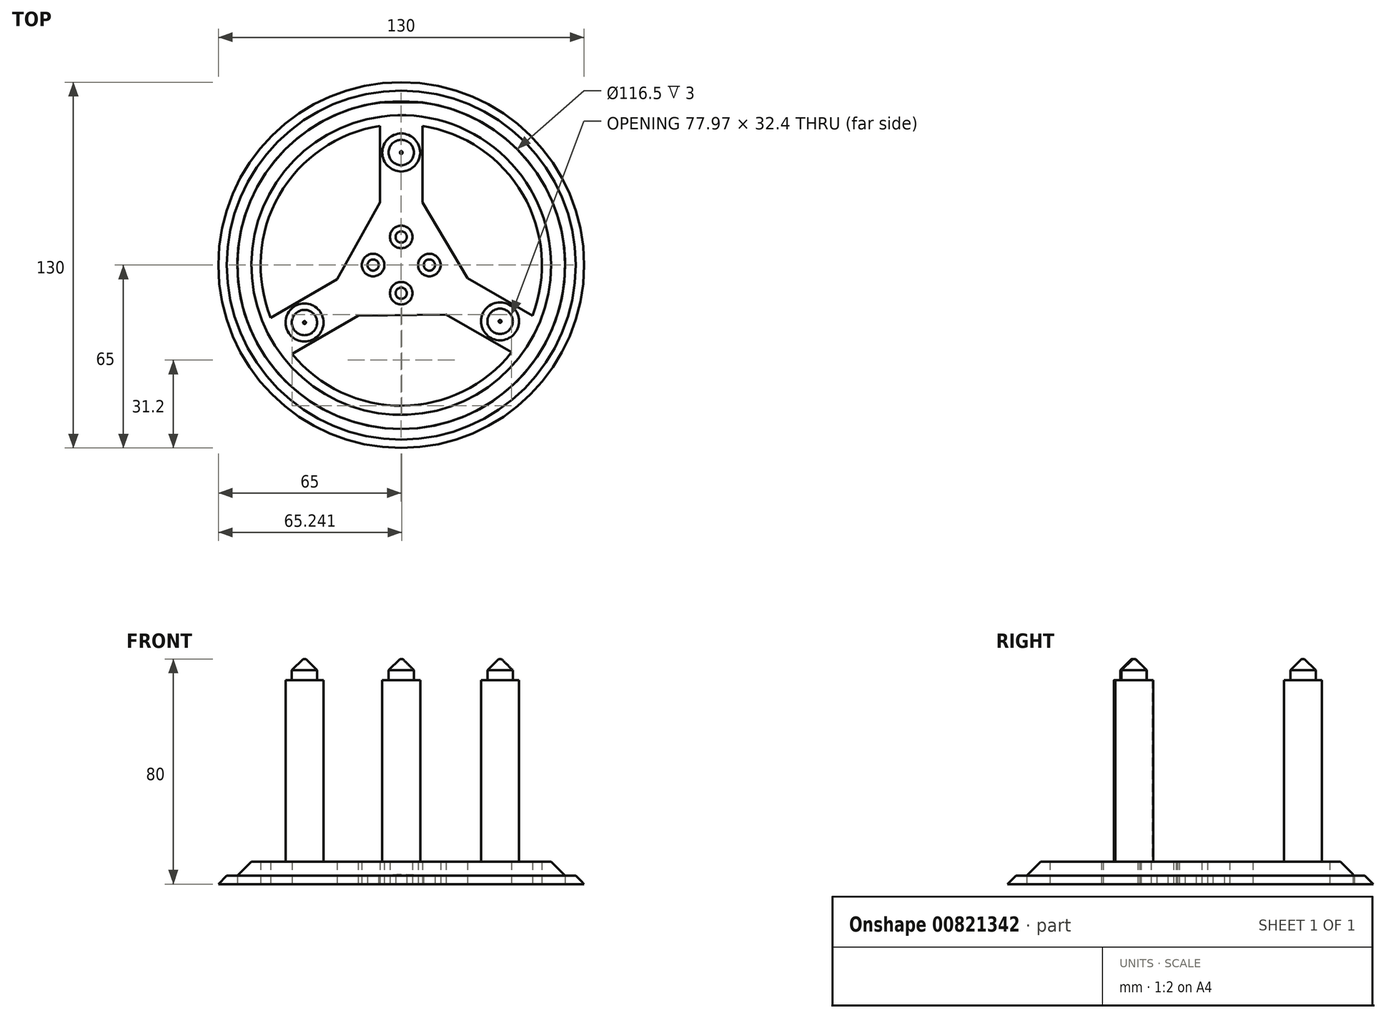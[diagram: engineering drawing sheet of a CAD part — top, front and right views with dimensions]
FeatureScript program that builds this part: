
annotation { "Feature Type Name" : "Feature", "Feature Type Description" : "" }
export const myFeature = defineFeature(function(context is Context, id is Id, definition is map)
    precondition{}
    {
        {
            var Q0;
            Q0=qCreatedBy(makeId("Top.planeOp"),FACE);
            var sketch = newSketch(context, id + "F0", { "sketchPlane" : qUnion([Q0])});
            skCircle(sketch, "E0", {"center": v(0, 0) * mm, "radius": 65 * mm});
            skCircle(sketch, "E1", {"center": v(0, 0) * mm, "radius": 50 * mm});
            skCircle(sketch, "E2", {"center": v(0, 0) * mm, "radius": 58.25 * mm});
            skLineSegment(sketch, "E3", {"start": v(0, 50) * mm, "end": v(0, 40) * mm});
            skCircle(sketch, "E4", {"center": v(0, 40) * mm, "radius": 6.75 * mm});
            skCircle(sketch, "E5", {"center": v(0, 40) * mm, "radius": 7.5 * mm});
            skLineSegment(sketch, "E6.bottom", {"start": v(7.5, 57.77) * mm, "end": v(-7.5, 57.77) * mm});
            skLineSegment(sketch, "E6.top", {"start": v(7.5, 22.23) * mm, "end": v(-7.5, 22.23) * mm});
            skLineSegment(sketch, "E6.left", {"start": v(7.5, 57.77) * mm, "end": v(7.5, 22.23) * mm});
            skLineSegment(sketch, "E6.right", {"start": v(-7.5, 57.77) * mm, "end": v(-7.5, 22.23) * mm});
            skCircle(sketch, "E7.1.0", {"center": v(35.14, -19.99) * mm, "radius": 7.5 * mm});
            skCircle(sketch, "E7.1.1", {"center": v(35.14, -19.99) * mm, "radius": 6.75 * mm});
            skLineSegment(sketch, "E7.1.2", {"start": v(54.28, -22.38) * mm, "end": v(23.5, -4.61) * mm});
            skLineSegment(sketch, "E7.1.3", {"start": v(46.78, -35.37) * mm, "end": v(16, -17.6) * mm});
            skCircle(sketch, "E7.2.0", {"center": v(-34.38, -20.43) * mm, "radius": 7.5 * mm});
            skCircle(sketch, "E7.2.1", {"center": v(-34.38, -20.43) * mm, "radius": 6.75 * mm});
            skLineSegment(sketch, "E7.2.2", {"start": v(-46.02, -35.8) * mm, "end": v(-15.25, -18.04) * mm});
            skLineSegment(sketch, "E7.2.3", {"start": v(-53.52, -22.81) * mm, "end": v(-22.75, -5.05) * mm});
            skPoint(sketch, "E7.center", {"position": v(0.25, -0.14) * mm});
            skLineSegment(sketch, "E7.anchor1", {"start": v(0.25, -0.14) * mm, "end": v(0, 40) * mm, "construction": true});
            skLineSegment(sketch, "E7.anchor2", {"start": v(0.25, -0.14) * mm, "end": v(-34.38, -20.43) * mm, "construction": true});
            skCircle(sketch, "E8", {"center": v(0, 40) * mm, "radius": 4.5 * mm});
            skCircle(sketch, "E9", {"center": v(-34.38, -20.43) * mm, "radius": 4.5 * mm});
            skCircle(sketch, "E10", {"center": v(35.14, -19.99) * mm, "radius": 4.5 * mm});
            skLineSegment(sketch, "E11", {"start": v(-22.75, -5.05) * mm, "end": v(-7.5, 22.23) * mm});
            skLineSegment(sketch, "E12", {"start": v(7.5, 22.23) * mm, "end": v(23.5, -4.61) * mm});
            skLineSegment(sketch, "E13", {"start": v(16, -17.6) * mm, "end": v(-15.25, -18.04) * mm});
            skCircle(sketch, "E14", {"center": v(0, 0) * mm, "radius": 7.5 * mm});
            skCircle(sketch, "E15", {"center": v(0, 0) * mm, "radius": 10 * mm});
            skLineSegment(sketch, "E16", {"start": v(0, -10) * mm, "end": v(0, 10) * mm});
            skLineSegment(sketch, "E17", {"start": v(-10, 0) * mm, "end": v(10, 0) * mm});
            skCircle(sketch, "E18", {"center": v(0, 10) * mm, "radius": 2 * mm});
            skCircle(sketch, "E19", {"center": v(-10, 0) * mm, "radius": 2 * mm});
            skCircle(sketch, "E20", {"center": v(10, 0) * mm, "radius": 2 * mm});
            skCircle(sketch, "E21", {"center": v(0, -10) * mm, "radius": 2 * mm});
            skCircle(sketch, "E22", {"center": v(0, 10) * mm, "radius": 4 * mm});
            skCircle(sketch, "E23", {"center": v(-10, 0) * mm, "radius": 4 * mm});
            skCircle(sketch, "E24", {"center": v(10, 0) * mm, "radius": 4 * mm});
            skCircle(sketch, "E25", {"center": v(0, -10) * mm, "radius": 4 * mm});
            skSolve(sketch);
        }
        {
            var Q0;
            {var subQ0=sQuery(id+"F0.wireOp",EDGE,"E20");var subQ1=sQuery(id+"F0.wireOp",EDGE,"E15");var subQ2=makeQuery(id+"F0.imprint","INTERSECT",VERTEX,{"disambiguationData":[OD(0.0)],"derivedFrom":[subQ1,subQ0]});Q0=makeQuery(id+"F0.imprint","IMPRINT",FACE,{"disambiguationData":[TD([[makeQuery(id+"F0.imprint","IMPRINT",EDGE,{"disambiguationData":[TD([[subQ2,-1.0]])],"derivedFrom":subQ1}),-1.0]])]});}
            var Q1;
            {var subQ5=sQuery(id+"F0.wireOp",EDGE,"E14");var subQ7=sQuery(id+"F0.wireOp",EDGE,"E24");var subQ9=makeQuery(id+"F0.imprint","INTERSECT",VERTEX,{"disambiguationData":[OD(0.0)],"derivedFrom":[subQ5,subQ7]});Q1=makeQuery(id+"F0.imprint","IMPRINT",FACE,{"disambiguationData":[TD([[makeQuery(id+"F0.imprint","IMPRINT",EDGE,{"disambiguationData":[TD([[subQ9,1.0]])],"derivedFrom":subQ5}),-1.0]])]});}
            var Q2;
            {var subQ0=sQuery(id+"F0.wireOp",EDGE,"E24");var subQ1=sQuery(id+"F0.wireOp",EDGE,"E14");var subQ2=makeQuery(id+"F0.imprint","INTERSECT",VERTEX,{"disambiguationData":[OD(0.0)],"derivedFrom":[subQ1,subQ0]});Q2=makeQuery(id+"F0.imprint","IMPRINT",FACE,{"disambiguationData":[TD([[makeQuery(id+"F0.imprint","IMPRINT",EDGE,{"disambiguationData":[TD([[subQ2,1.0]])],"derivedFrom":subQ1}),1.0]])]});}
            var Q3;
            {var subQ0=sQuery(id+"F0.wireOp",EDGE,"E17");var subQ1=sQuery(id+"F0.wireOp",EDGE,"E14");var subQ2=makeQuery(id+"F0.imprint","INTERSECT",VERTEX,{"disambiguationData":[OD(0.0)],"derivedFrom":[subQ1,subQ0]});Q3=makeQuery(id+"F0.imprint","IMPRINT",FACE,{"disambiguationData":[TD([[makeQuery(id+"F0.imprint","IMPRINT",EDGE,{"disambiguationData":[TD([[subQ2,1.0]])],"derivedFrom":subQ1}),1.0]])]});}
            var Q4;
            {var subQ3=sQuery(id+"F0.wireOp",EDGE,"E17");var subQ5=sQuery(id+"F0.wireOp",EDGE,"E14");var subQ6=makeQuery(id+"F0.imprint","INTERSECT",VERTEX,{"disambiguationData":[OD(0.0)],"derivedFrom":[subQ5,subQ3]});Q4=makeQuery(id+"F0.imprint","IMPRINT",FACE,{"disambiguationData":[TD([[makeQuery(id+"F0.imprint","IMPRINT",EDGE,{"disambiguationData":[TD([[subQ6,1.0]])],"derivedFrom":subQ5}),-1.0]])]});}
            var Q5;
            {var subQ0=sQuery(id+"F0.wireOp",EDGE,"E22");var subQ1=sQuery(id+"F0.wireOp",EDGE,"E15");var subQ2=makeQuery(id+"F0.imprint","INTERSECT",VERTEX,{"disambiguationData":[OD(0.0)],"derivedFrom":[subQ1,subQ0]});Q5=makeQuery(id+"F0.imprint","IMPRINT",FACE,{"disambiguationData":[TD([[makeQuery(id+"F0.imprint","IMPRINT",EDGE,{"disambiguationData":[TD([[subQ2,-1.0]])],"derivedFrom":subQ1}),-1.0]])]});}
            var Q6;
            {var subQ5=sQuery(id+"F0.wireOp",EDGE,"E14");var subQ7=sQuery(id+"F0.wireOp",EDGE,"E22");var subQ9=makeQuery(id+"F0.imprint","INTERSECT",VERTEX,{"disambiguationData":[OD(0.0)],"derivedFrom":[subQ5,subQ7]});Q6=makeQuery(id+"F0.imprint","IMPRINT",FACE,{"disambiguationData":[TD([[makeQuery(id+"F0.imprint","IMPRINT",EDGE,{"disambiguationData":[TD([[subQ9,-1.0]])],"derivedFrom":subQ5}),-1.0]])]});}
            var Q7;
            {var subQ0=sQuery(id+"F0.wireOp",EDGE,"E22");var subQ1=sQuery(id+"F0.wireOp",EDGE,"E14");var subQ2=makeQuery(id+"F0.imprint","INTERSECT",VERTEX,{"disambiguationData":[OD(0.0)],"derivedFrom":[subQ1,subQ0]});Q7=makeQuery(id+"F0.imprint","IMPRINT",FACE,{"disambiguationData":[TD([[makeQuery(id+"F0.imprint","IMPRINT",EDGE,{"disambiguationData":[TD([[subQ2,-1.0]])],"derivedFrom":subQ1}),1.0]])]});}
            var Q8;
            {var subQ0=sQuery(id+"F0.wireOp",EDGE,"E16");var subQ1=sQuery(id+"F0.wireOp",EDGE,"E14");var subQ2=makeQuery(id+"F0.imprint","INTERSECT",VERTEX,{"disambiguationData":[OD(0.0)],"derivedFrom":[subQ1,subQ0]});Q8=makeQuery(id+"F0.imprint","IMPRINT",FACE,{"disambiguationData":[TD([[makeQuery(id+"F0.imprint","IMPRINT",EDGE,{"disambiguationData":[TD([[subQ2,-1.0]])],"derivedFrom":subQ1}),1.0]])]});}
            var Q9;
            {var subQ3=sQuery(id+"F0.wireOp",EDGE,"E16");var subQ5=sQuery(id+"F0.wireOp",EDGE,"E14");var subQ6=makeQuery(id+"F0.imprint","INTERSECT",VERTEX,{"disambiguationData":[OD(0.0)],"derivedFrom":[subQ5,subQ3]});Q9=makeQuery(id+"F0.imprint","IMPRINT",FACE,{"disambiguationData":[TD([[makeQuery(id+"F0.imprint","IMPRINT",EDGE,{"disambiguationData":[TD([[subQ6,-1.0]])],"derivedFrom":subQ5}),-1.0]])]});}
            var Q10;
            {var subQ0=sQuery(id+"F0.wireOp",EDGE,"E23");var subQ1=sQuery(id+"F0.wireOp",EDGE,"E15");var subQ2=makeQuery(id+"F0.imprint","INTERSECT",VERTEX,{"disambiguationData":[OD(0.0)],"derivedFrom":[subQ1,subQ0]});Q10=makeQuery(id+"F0.imprint","IMPRINT",FACE,{"disambiguationData":[TD([[makeQuery(id+"F0.imprint","IMPRINT",EDGE,{"disambiguationData":[TD([[subQ2,-1.0]])],"derivedFrom":subQ1}),-1.0]])]});}
            var Q11;
            {var subQ5=sQuery(id+"F0.wireOp",EDGE,"E14");var subQ7=sQuery(id+"F0.wireOp",EDGE,"E23");var subQ9=makeQuery(id+"F0.imprint","INTERSECT",VERTEX,{"disambiguationData":[OD(0.0)],"derivedFrom":[subQ5,subQ7]});Q11=makeQuery(id+"F0.imprint","IMPRINT",FACE,{"disambiguationData":[TD([[makeQuery(id+"F0.imprint","IMPRINT",EDGE,{"disambiguationData":[TD([[subQ9,-1.0]])],"derivedFrom":subQ5}),-1.0]])]});}
            var Q12;
            {var subQ0=sQuery(id+"F0.wireOp",EDGE,"E17");var subQ1=sQuery(id+"F0.wireOp",EDGE,"E14");var subQ2=makeQuery(id+"F0.imprint","INTERSECT",VERTEX,{"disambiguationData":[OD(1.0)],"derivedFrom":[subQ1,subQ0]});Q12=makeQuery(id+"F0.imprint","IMPRINT",FACE,{"disambiguationData":[TD([[makeQuery(id+"F0.imprint","IMPRINT",EDGE,{"disambiguationData":[TD([[subQ2,-1.0]])],"derivedFrom":subQ1}),1.0]])]});}
            var Q13;
            {var subQ0=sQuery(id+"F0.wireOp",EDGE,"E23");var subQ1=sQuery(id+"F0.wireOp",EDGE,"E14");var subQ2=makeQuery(id+"F0.imprint","INTERSECT",VERTEX,{"disambiguationData":[OD(0.0)],"derivedFrom":[subQ1,subQ0]});Q13=makeQuery(id+"F0.imprint","IMPRINT",FACE,{"disambiguationData":[TD([[makeQuery(id+"F0.imprint","IMPRINT",EDGE,{"disambiguationData":[TD([[subQ2,-1.0]])],"derivedFrom":subQ1}),1.0]])]});}
            var Q14;
            {var subQ3=sQuery(id+"F0.wireOp",EDGE,"E17");var subQ7=sQuery(id+"F0.wireOp",EDGE,"E14");var subQ8=makeQuery(id+"F0.imprint","INTERSECT",VERTEX,{"disambiguationData":[OD(1.0)],"derivedFrom":[subQ7,subQ3]});Q14=makeQuery(id+"F0.imprint","IMPRINT",FACE,{"disambiguationData":[TD([[makeQuery(id+"F0.imprint","IMPRINT",EDGE,{"disambiguationData":[TD([[subQ8,-1.0]])],"derivedFrom":subQ7}),-1.0]])]});}
            var Q15;
            {var subQ3=sQuery(id+"F0.wireOp",EDGE,"E16");var subQ5=sQuery(id+"F0.wireOp",EDGE,"E14");var subQ6=makeQuery(id+"F0.imprint","INTERSECT",VERTEX,{"disambiguationData":[OD(1.0)],"derivedFrom":[subQ5,subQ3]});Q15=makeQuery(id+"F0.imprint","IMPRINT",FACE,{"disambiguationData":[TD([[makeQuery(id+"F0.imprint","IMPRINT",EDGE,{"disambiguationData":[TD([[subQ6,-1.0]])],"derivedFrom":subQ5}),-1.0]])]});}
            var Q16;
            {var subQ0=sQuery(id+"F0.wireOp",EDGE,"E25");var subQ1=sQuery(id+"F0.wireOp",EDGE,"E15");var subQ2=makeQuery(id+"F0.imprint","INTERSECT",VERTEX,{"disambiguationData":[OD(0.0)],"derivedFrom":[subQ1,subQ0]});Q16=makeQuery(id+"F0.imprint","IMPRINT",FACE,{"disambiguationData":[TD([[makeQuery(id+"F0.imprint","IMPRINT",EDGE,{"disambiguationData":[TD([[subQ2,-1.0]])],"derivedFrom":subQ1}),-1.0]])]});}
            var Q17;
            {var subQ0=sQuery(id+"F0.wireOp",EDGE,"E25");var subQ7=sQuery(id+"F0.wireOp",EDGE,"E14");var subQ9=makeQuery(id+"F0.imprint","INTERSECT",VERTEX,{"disambiguationData":[OD(0.0)],"derivedFrom":[subQ7,subQ0]});Q17=makeQuery(id+"F0.imprint","IMPRINT",FACE,{"disambiguationData":[TD([[makeQuery(id+"F0.imprint","IMPRINT",EDGE,{"disambiguationData":[TD([[subQ9,-1.0]])],"derivedFrom":subQ7}),-1.0]])]});}
            var Q18;
            {var subQ0=sQuery(id+"F0.wireOp",EDGE,"E25");var subQ1=sQuery(id+"F0.wireOp",EDGE,"E14");var subQ2=makeQuery(id+"F0.imprint","INTERSECT",VERTEX,{"disambiguationData":[OD(0.0)],"derivedFrom":[subQ1,subQ0]});Q18=makeQuery(id+"F0.imprint","IMPRINT",FACE,{"disambiguationData":[TD([[makeQuery(id+"F0.imprint","IMPRINT",EDGE,{"disambiguationData":[TD([[subQ2,-1.0]])],"derivedFrom":subQ1}),1.0]])]});}
            var Q19;
            {var subQ0=sQuery(id+"F0.wireOp",EDGE,"E16");var subQ1=sQuery(id+"F0.wireOp",EDGE,"E14");var subQ2=makeQuery(id+"F0.imprint","INTERSECT",VERTEX,{"disambiguationData":[OD(1.0)],"derivedFrom":[subQ1,subQ0]});Q19=makeQuery(id+"F0.imprint","IMPRINT",FACE,{"disambiguationData":[TD([[makeQuery(id+"F0.imprint","IMPRINT",EDGE,{"disambiguationData":[TD([[subQ2,-1.0]])],"derivedFrom":subQ1}),1.0]])]});}
            var Q20;
            Q20=makeQuery(id+"F0.imprint","IMPRINT",FACE,{"disambiguationData":[TD([[makeQuery(id+"F0.imprint","IMPRINT",EDGE,{"derivedFrom":sQuery(id+"F0.wireOp",EDGE,"E0")}),1.0]])]});
            extrude(context, id + "F1", {"entities" : qUnion([Q0, Q1, Q2, Q3, Q4, Q5, Q6, Q7, Q8, Q9, Q10, Q11, Q12, Q13, Q14, Q15, Q16, Q17, Q18, Q19, Q20]), "depth" : 3 * mm, "offsetDistance" : 25 * mm});
        }
        {
            var Q0;
            Q0=makeQuery(id+"F1.opExtrude","CAP_EDGE",EDGE,{"disambiguationData":[OSD([sQuery(id+"F0.wireOp",EDGE,"E0")])],"isStart":false});
            chamfer(context, id + "F2", {"entities" : qUnion([Q0]), "width" : 3 * mm, "tangentPropagation" : true});
        }
        {
            var Q0;
            {var subQ5=sQuery(id+"F0.wireOp",EDGE,"E1");var subQ6=makeQuery(id+"F0.imprint","INTERSECT",VERTEX,{"derivedFrom":[subQ5,sQuery(id+"F0.wireOp",EDGE,"E7.2.3")]});Q0=makeQuery(id+"F0.imprint","IMPRINT",FACE,{"disambiguationData":[TD([[makeQuery(id+"F0.imprint","IMPRINT",EDGE,{"disambiguationData":[TD([[subQ6,1.0]])],"derivedFrom":subQ5}),-1.0]])]});}
            var Q1;
            {var subQ1=sQuery(id+"F0.wireOp",EDGE,"E6.bottom");Q1=makeQuery(id+"F0.imprint","IMPRINT",FACE,{"disambiguationData":[TD([[makeQuery(id+"F0.imprint","IMPRINT",EDGE,{"derivedFrom":subQ1}),1.0]])]});}
            var Q2;
            {var subQ0=sQuery(id+"F0.wireOp",EDGE,"E6.left");var subQ1=sQuery(id+"F0.wireOp",EDGE,"E1");var subQ2=makeQuery(id+"F0.imprint","INTERSECT",VERTEX,{"derivedFrom":[subQ1,subQ0]});Q2=makeQuery(id+"F0.imprint","IMPRINT",FACE,{"disambiguationData":[TD([[makeQuery(id+"F0.imprint","IMPRINT",EDGE,{"disambiguationData":[TD([[subQ2,1.0]])],"derivedFrom":subQ1}),-1.0]])]});}
            var Q3;
            {var subQ0=sQuery(id+"F0.wireOp",EDGE,"E7.2.2");var subQ1=sQuery(id+"F0.wireOp",EDGE,"E1");var subQ2=makeQuery(id+"F0.imprint","INTERSECT",VERTEX,{"derivedFrom":[subQ1,subQ0]});Q3=makeQuery(id+"F0.imprint","IMPRINT",FACE,{"disambiguationData":[TD([[makeQuery(id+"F0.imprint","IMPRINT",EDGE,{"disambiguationData":[TD([[subQ2,-1.0]])],"derivedFrom":subQ1}),-1.0]])]});}
            var Q4;
            {var subQ0=sQuery(id+"F0.wireOp",EDGE,"E7.1.3");var subQ1=sQuery(id+"F0.wireOp",EDGE,"E1");var subQ2=makeQuery(id+"F0.imprint","INTERSECT",VERTEX,{"derivedFrom":[subQ1,subQ0]});Q4=makeQuery(id+"F0.imprint","IMPRINT",FACE,{"disambiguationData":[TD([[makeQuery(id+"F0.imprint","IMPRINT",EDGE,{"disambiguationData":[TD([[subQ2,-1.0]])],"derivedFrom":subQ1}),-1.0]])]});}
            var Q5;
            Q5=makeQuery(id+"F0.imprint","IMPRINT",FACE,{"disambiguationData":[TD([[makeQuery(id+"F0.imprint","IMPRINT",EDGE,{"derivedFrom":sQuery(id+"F0.wireOp",EDGE,"E6.top")}),1.0]])]});
            var Q6;
            {var subQ0=sQuery(id+"F0.wireOp",EDGE,"E7.2.3");var subQ1=sQuery(id+"F0.wireOp",EDGE,"E1");var subQ2=makeQuery(id+"F0.imprint","INTERSECT",VERTEX,{"derivedFrom":[subQ1,subQ0]});Q6=makeQuery(id+"F0.imprint","IMPRINT",FACE,{"disambiguationData":[TD([[makeQuery(id+"F0.imprint","IMPRINT",EDGE,{"disambiguationData":[TD([[subQ2,-1.0]])],"derivedFrom":subQ1}),1.0]])]});}
            var Q7;
            {var subQ0=sQuery(id+"F0.wireOp",EDGE,"E7.1.3");var subQ1=sQuery(id+"F0.wireOp",EDGE,"E1");var subQ2=makeQuery(id+"F0.imprint","INTERSECT",VERTEX,{"derivedFrom":[subQ1,subQ0]});Q7=makeQuery(id+"F0.imprint","IMPRINT",FACE,{"disambiguationData":[TD([[makeQuery(id+"F0.imprint","IMPRINT",EDGE,{"disambiguationData":[TD([[subQ2,-1.0]])],"derivedFrom":subQ1}),1.0]])]});}
            var Q8;
            {var subQ5=sQuery(id+"F0.wireOp",EDGE,"E6.top");Q8=makeQuery(id+"F0.imprint","IMPRINT",FACE,{"disambiguationData":[TD([[makeQuery(id+"F0.imprint","IMPRINT",EDGE,{"derivedFrom":subQ5}),-1.0]])]});}
            var Q9;
            {var subQ0=sQuery(id+"F0.wireOp",EDGE,"E3");var subQ1=sQuery(id+"F0.wireOp",EDGE,"E1");var subQ2=makeQuery(id+"F0.imprint","INTERSECT",VERTEX,{"derivedFrom":[subQ1,subQ0]});Q9=makeQuery(id+"F0.imprint","IMPRINT",FACE,{"disambiguationData":[TD([[makeQuery(id+"F0.imprint","IMPRINT",EDGE,{"disambiguationData":[TD([[subQ2,1.0]])],"derivedFrom":subQ1}),1.0]])]});}
            var Q10;
            {var subQ0=sQuery(id+"F0.wireOp",EDGE,"E3");var subQ1=sQuery(id+"F0.wireOp",EDGE,"E1");var subQ2=makeQuery(id+"F0.imprint","INTERSECT",VERTEX,{"derivedFrom":[subQ1,subQ0]});Q10=makeQuery(id+"F0.imprint","IMPRINT",FACE,{"disambiguationData":[TD([[makeQuery(id+"F0.imprint","IMPRINT",EDGE,{"disambiguationData":[TD([[subQ2,-1.0]])],"derivedFrom":subQ1}),1.0]])]});}
            var Q11;
            {var subQ0=sQuery(id+"F0.wireOp",EDGE,"E24");var subQ1=sQuery(id+"F0.wireOp",EDGE,"E14");var subQ2=makeQuery(id+"F0.imprint","INTERSECT",VERTEX,{"disambiguationData":[OD(0.0)],"derivedFrom":[subQ1,subQ0]});Q11=makeQuery(id+"F0.imprint","IMPRINT",FACE,{"disambiguationData":[TD([[makeQuery(id+"F0.imprint","IMPRINT",EDGE,{"disambiguationData":[TD([[subQ2,-1.0]])],"derivedFrom":subQ1}),-1.0]])]});}
            var Q12;
            {var subQ1=sQuery(id+"F0.wireOp",EDGE,"E14");var subQ7=sQuery(id+"F0.wireOp",EDGE,"E24");var subQ9=makeQuery(id+"F0.imprint","INTERSECT",VERTEX,{"disambiguationData":[OD(0.0)],"derivedFrom":[subQ1,subQ7]});Q12=makeQuery(id+"F0.imprint","IMPRINT",FACE,{"disambiguationData":[TD([[makeQuery(id+"F0.imprint","IMPRINT",EDGE,{"disambiguationData":[TD([[subQ9,-1.0]])],"derivedFrom":subQ1}),1.0]])]});}
            var Q13;
            {var subQ1=sQuery(id+"F0.wireOp",EDGE,"E14");var subQ7=sQuery(id+"F0.wireOp",EDGE,"E25");var subQ9=makeQuery(id+"F0.imprint","INTERSECT",VERTEX,{"disambiguationData":[OD(1.0)],"derivedFrom":[subQ1,subQ7]});Q13=makeQuery(id+"F0.imprint","IMPRINT",FACE,{"disambiguationData":[TD([[makeQuery(id+"F0.imprint","IMPRINT",EDGE,{"disambiguationData":[TD([[subQ9,-1.0]])],"derivedFrom":subQ1}),1.0]])]});}
            var Q14;
            {var subQ0=sQuery(id+"F0.wireOp",EDGE,"E25");var subQ1=sQuery(id+"F0.wireOp",EDGE,"E14");var subQ2=makeQuery(id+"F0.imprint","INTERSECT",VERTEX,{"disambiguationData":[OD(1.0)],"derivedFrom":[subQ1,subQ0]});Q14=makeQuery(id+"F0.imprint","IMPRINT",FACE,{"disambiguationData":[TD([[makeQuery(id+"F0.imprint","IMPRINT",EDGE,{"disambiguationData":[TD([[subQ2,-1.0]])],"derivedFrom":subQ1}),-1.0]])]});}
            var Q15;
            {var subQ0=sQuery(id+"F0.wireOp",EDGE,"E23");var subQ1=sQuery(id+"F0.wireOp",EDGE,"E14");var subQ2=makeQuery(id+"F0.imprint","INTERSECT",VERTEX,{"disambiguationData":[OD(1.0)],"derivedFrom":[subQ1,subQ0]});Q15=makeQuery(id+"F0.imprint","IMPRINT",FACE,{"disambiguationData":[TD([[makeQuery(id+"F0.imprint","IMPRINT",EDGE,{"disambiguationData":[TD([[subQ2,-1.0]])],"derivedFrom":subQ1}),-1.0]])]});}
            var Q16;
            {var subQ5=sQuery(id+"F0.wireOp",EDGE,"E14");var subQ7=sQuery(id+"F0.wireOp",EDGE,"E22");var subQ8=makeQuery(id+"F0.imprint","INTERSECT",VERTEX,{"disambiguationData":[OD(1.0)],"derivedFrom":[subQ5,subQ7]});Q16=makeQuery(id+"F0.imprint","IMPRINT",FACE,{"disambiguationData":[TD([[makeQuery(id+"F0.imprint","IMPRINT",EDGE,{"disambiguationData":[TD([[subQ8,-1.0]])],"derivedFrom":subQ5}),1.0]])]});}
            var Q17;
            {var subQ0=sQuery(id+"F0.wireOp",EDGE,"E23");var subQ1=sQuery(id+"F0.wireOp",EDGE,"E14");var subQ2=makeQuery(id+"F0.imprint","INTERSECT",VERTEX,{"disambiguationData":[OD(1.0)],"derivedFrom":[subQ1,subQ0]});Q17=makeQuery(id+"F0.imprint","IMPRINT",FACE,{"disambiguationData":[TD([[makeQuery(id+"F0.imprint","IMPRINT",EDGE,{"disambiguationData":[TD([[subQ2,-1.0]])],"derivedFrom":subQ1}),1.0]])]});}
            var Q18;
            {var subQ0=sQuery(id+"F0.wireOp",EDGE,"E22");var subQ1=sQuery(id+"F0.wireOp",EDGE,"E14");var subQ2=makeQuery(id+"F0.imprint","INTERSECT",VERTEX,{"disambiguationData":[OD(1.0)],"derivedFrom":[subQ1,subQ0]});Q18=makeQuery(id+"F0.imprint","IMPRINT",FACE,{"disambiguationData":[TD([[makeQuery(id+"F0.imprint","IMPRINT",EDGE,{"disambiguationData":[TD([[subQ2,-1.0]])],"derivedFrom":subQ1}),-1.0]])]});}
            var Q19;
            Q19=makeQuery(id+"F0.imprint","IMPRINT",FACE,{"disambiguationData":[TD([[makeQuery(id+"F0.imprint","IMPRINT",EDGE,{"derivedFrom":sQuery(id+"F0.wireOp",EDGE,"E4")}),-1.0]])]});
            var Q20;
            Q20=makeQuery(id+"F0.imprint","IMPRINT",FACE,{"disambiguationData":[TD([[makeQuery(id+"F0.imprint","IMPRINT",EDGE,{"derivedFrom":sQuery(id+"F0.wireOp",EDGE,"E7.2.1")}),-1.0]])]});
            var Q21;
            Q21=makeQuery(id+"F0.imprint","IMPRINT",FACE,{"disambiguationData":[TD([[makeQuery(id+"F0.imprint","IMPRINT",EDGE,{"derivedFrom":sQuery(id+"F0.wireOp",EDGE,"E7.1.1")}),-1.0]])]});
            extrude(context, id + "F3", {"entities" : qUnion([Q0, Q1, Q2, Q3, Q4, Q5, Q6, Q7, Q8, Q9, Q10, Q11, Q12, Q13, Q14, Q15, Q16, Q17, Q18, Q19, Q20, Q21]), "depth" : 8 * mm, "offsetDistance" : 25 * mm});
        }
        {
            var Q0;
            Q0=makeQuery(id+"F3.opExtrude","CAP_EDGE",EDGE,{"disambiguationData":[OSD([sQuery(id+"F0.wireOp",EDGE,"E2")])],"isStart":false});
            chamfer(context, id + "F4", {"entities" : qUnion([Q0]), "width" : 5 * mm, "tangentPropagation" : true});
        }
        {
            var Q0;
            Q0=makeQuery(id+"F0.imprint","IMPRINT",FACE,{"disambiguationData":[TD([[makeQuery(id+"F0.imprint","IMPRINT",EDGE,{"derivedFrom":sQuery(id+"F0.wireOp",EDGE,"E4")}),1.0]])]});
            var Q1;
            Q1=makeQuery(id+"F0.imprint","IMPRINT",FACE,{"disambiguationData":[TD([[makeQuery(id+"F0.imprint","IMPRINT",EDGE,{"derivedFrom":sQuery(id+"F0.wireOp",EDGE,"E7.2.1")}),1.0]])]});
            var Q2;
            Q2=makeQuery(id+"F0.imprint","IMPRINT",FACE,{"disambiguationData":[TD([[makeQuery(id+"F0.imprint","IMPRINT",EDGE,{"derivedFrom":sQuery(id+"F0.wireOp",EDGE,"E7.1.1")}),1.0]])]});
            extrude(context, id + "F5", {"entities" : qUnion([Q0, Q1, Q2]), "operationType" : NewBodyOperationType.ADD, "depth" : 72.5 * mm, "offsetDistance" : 25 * mm});
        }
        {
            var Q0;
            Q0=makeQuery(id+"F0.imprint","IMPRINT",FACE,{"disambiguationData":[TD([[makeQuery(id+"F0.imprint","IMPRINT",EDGE,{"derivedFrom":sQuery(id+"F0.wireOp",EDGE,"E8")}),1.0]])]});
            var Q1;
            Q1=makeQuery(id+"F0.imprint","IMPRINT",FACE,{"disambiguationData":[TD([[makeQuery(id+"F0.imprint","IMPRINT",EDGE,{"derivedFrom":sQuery(id+"F0.wireOp",EDGE,"E9")}),1.0]])]});
            var Q2;
            Q2=makeQuery(id+"F0.imprint","IMPRINT",FACE,{"disambiguationData":[TD([[makeQuery(id+"F0.imprint","IMPRINT",EDGE,{"derivedFrom":sQuery(id+"F0.wireOp",EDGE,"E10")}),1.0]])]});
            extrude(context, id + "F6", {"entities" : qUnion([Q0, Q1, Q2]), "operationType" : NewBodyOperationType.ADD, "depth" : 80 * mm, "offsetDistance" : 25 * mm});
        }
        {
            var Q0;
            Q0=makeQuery(id+"F6.opExtrude","CAP_EDGE",EDGE,{"disambiguationData":[OSD([sQuery(id+"F0.wireOp",EDGE,"E8")])],"isStart":false});
            var Q1;
            Q1=makeQuery(id+"F6.opExtrude","CAP_EDGE",EDGE,{"disambiguationData":[OSD([sQuery(id+"F0.wireOp",EDGE,"E9")])],"isStart":false});
            var Q2;
            Q2=makeQuery(id+"F6.opExtrude","CAP_EDGE",EDGE,{"disambiguationData":[OSD([sQuery(id+"F0.wireOp",EDGE,"E10")])],"isStart":false});
            chamfer(context, id + "F7", {"entities" : qUnion([Q0, Q1, Q2]), "width" : 4 * mm, "tangentPropagation" : true});
        }
    });
